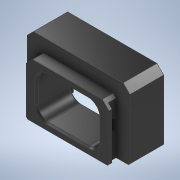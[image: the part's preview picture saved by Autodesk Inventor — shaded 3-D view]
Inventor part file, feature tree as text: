
AUTODESK INVENTOR PART (.ipt)
format: ipt  version: 2020.2 (Build 242310000, 310)  size: 747,520 bytes
history: native  units: mm
features: fillet x9, extrude x7, sketch x7, projected_geometry x3, chamfer x2, mirror x1
ambient origin geometry x8: Origin, YZ Plane, XZ Plane, XY Plane, X Axis, Y Axis, Z Axis, Center Point
bodies: Solid1 (feature_tree)
feature tree (29):
  extrude  "Extrusion1"  Depth=20.0mm
  extrude  "Extrusion2"  Depth=12.0mm
  extrude  "Extrusion3"  Depth=22.0mm
  extrude  "Extrusion4"  Depth=2.2mm TaperAngle=0.0deg
  extrude  "Extrusion5"  Depth=1.0mm TaperAngle=0.0deg
  extrude  "Extrusion6"  Depth=0.6mm TaperAngle=0.0deg
  fillet  "Fillet3"  Radius=6.8mm
  fillet  "Fillet1"  Radius=1.5mm
  mirror  "Mirror1"
  chamfer  "Chamfer1"  Distance=16.0mm
  chamfer  "Chamfer2"  Distance=3.0mm
  extrude  "Extrusion7"  Depth=22.6mm
  fillet  "Fillet4"  Radius=11.3mm
  fillet  "Fillet5"  Radius=21.6mm
  fillet  "Fillet6"  Radius=10.8mm
  fillet  "Fillet7"  [1 undecoded]
  fillet  "Fillet8"  [1 undecoded]
  fillet  "Fillet9"  [1 undecoded]
  fillet  "Fillet10"  [1 undecoded]
  sketch  "Sketch1"  dims[d0=30.0mm d1=20.0mm]
  sketch  "Sketch2"  dims[d2=18.0mm d3=12.0mm]
  projected_geometry  "Projected Loop1"
  sketch  "Sketch3"  dims[d4=7.0mm d5=0.0mm d6=22.0mm]
  sketch  "Sketch4"  dims[d7=16.0mm d8=2.2mm d9=0.0mm]
  projected_geometry  "Projected Loop2"
  sketch  "Sketch5"  dims[d10=24.2mm d11=1.0mm d12=0.0mm]
  projected_geometry  "Projected Loop3"
  sketch  "Sketch6"  dims[d13=2.0mm d17=0.6mm d18=0.0mm d19=6.8mm d20=1.5mm]
  sketch  "Sketch8"  dims[d21=25.0mm d22=16.0mm d23=3.0mm d24=0.0mm d26=22.6mm d27=11.3mm d28=21.6mm d29=10.8mm d30=45.0deg d31=45.0deg d32=45.0deg d33=45.0deg d34=7.5mm d35=2.0mm d36=1.4mm d37=0.0mm d38=3.0mm d40=2.0mm d41=2.0mm d42=2.0mm d43=45.0deg d44=0.5mm d45=2.0mm d46=45.0deg d47=10.0mm d48=0.0mm d49=0.1mm d50=0.1mm d51=0.1mm d52=0.1mm d53=0.1mm d54=0.1mm d55=0.1mm]
note: 4 required parameter values undecoded (feature->parameter linkage not recoverable at this tier; creation-order binding heuristic only, values carry confidence <= 0.55)
